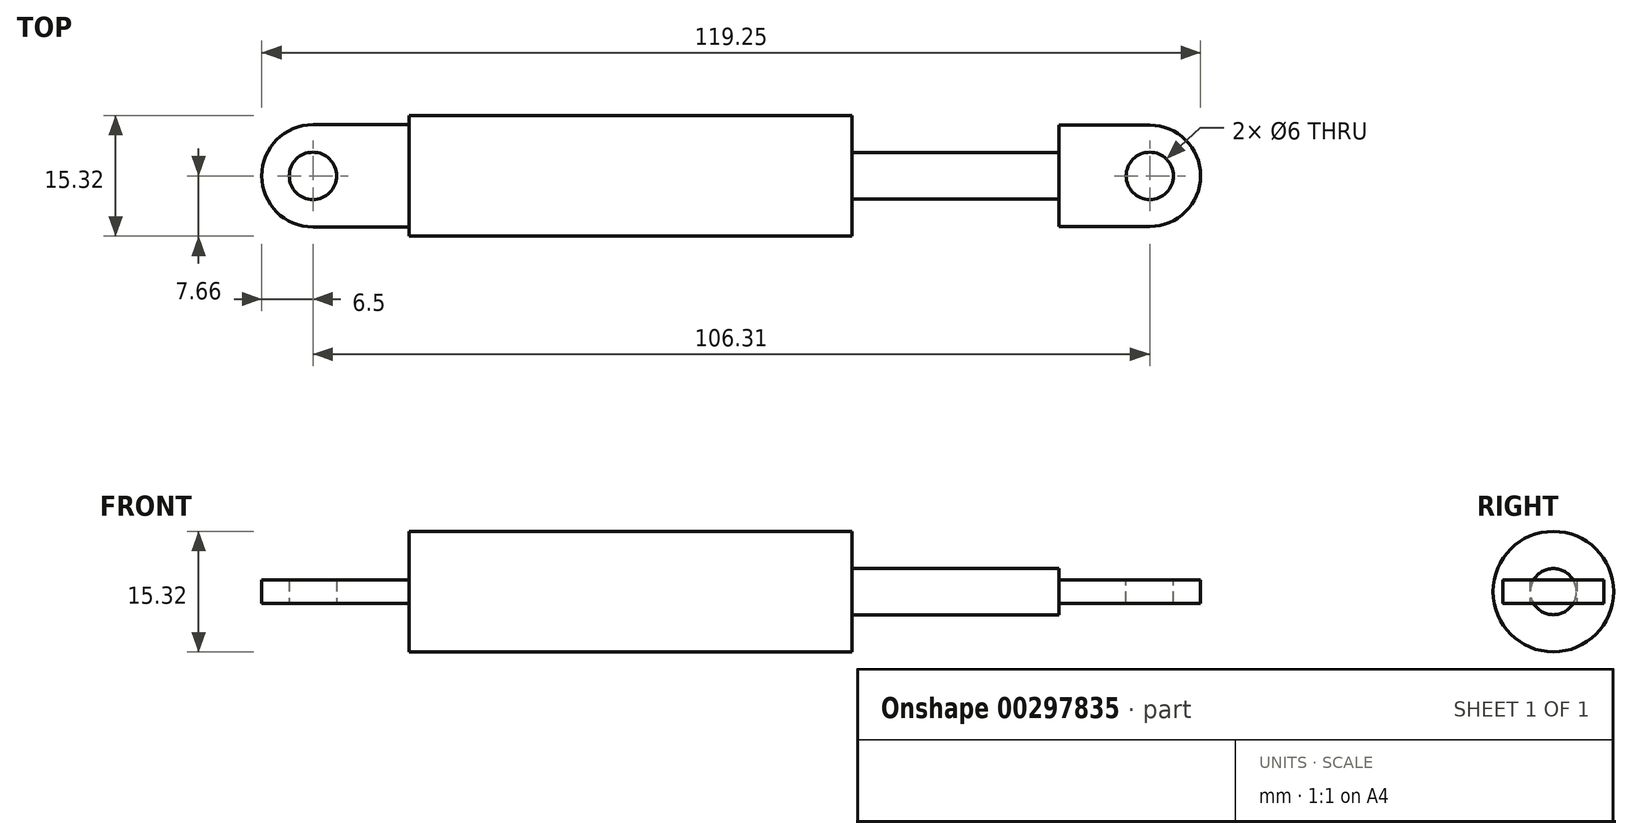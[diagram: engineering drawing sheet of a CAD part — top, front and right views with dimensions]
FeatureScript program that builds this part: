
annotation { "Feature Type Name" : "Feature", "Feature Type Description" : "" }
export const myFeature = defineFeature(function(context is Context, id is Id, definition is map)
    precondition{}
    {
        {
            var Q0;
            Q0=qCreatedBy(makeId("Top.planeOp"),FACE);
            var sketch = newSketch(context, id + "F0", { "sketchPlane" : qUnion([Q0])});
            skLineSegment(sketch, "E0.bottom", {"start": v(9.35, -6.5) * mm, "end": v(-2.85, -6.5) * mm});
            skLineSegment(sketch, "E0.top", {"start": v(9.35, 6.5) * mm, "end": v(-2.85, 6.5) * mm});
            skLineSegment(sketch, "E0.left", {"start": v(9.35, -6.5) * mm, "end": v(9.35, 6.5) * mm});
            skPoint(sketch, "E0.middle", {"position": v(0, 0) * mm});
            skArc(sketch, "E1", {"start": v(-2.85, 6.5) * mm, "mid": v(-9.35, 0) * mm, "end": v(-2.85, -6.5) * mm});
            skCircle(sketch, "E2", {"center": v(-2.85, 0) * mm, "radius": 3 * mm});
            skSolve(sketch);
        }
        {
            var Q0;
            Q0=makeQuery(id+"F0.imprint","IMPRINT",FACE,{"disambiguationData":[TD([[makeQuery(id+"F0.imprint","IMPRINT",EDGE,{"derivedFrom":sQuery(id+"F0.wireOp",EDGE,"E0.bottom")}),-1.0]])]});
            extrude(context, id + "F1", {"entities" : qUnion([Q0]), "endBound" : BoundingType.SYMMETRIC, "depth" : 3 * mm});
        }
        {
            var Q0;
            Q0=makeQuery(id+"F1.opExtrude","SWEPT_FACE",FACE,{"disambiguationData":[OSD([sQuery(id+"F0.wireOp",EDGE,"E0.left")])]});
            var sketch = newSketch(context, id + "F2", { "sketchPlane" : qUnion([Q0])});
            skCircle(sketch, "E3", {"center": v(0, 0) * mm, "radius": 7.66 * mm});
            skSolve(sketch);
        }
        {
            var Q0;
            Q0=makeQuery(id+"F2.imprint","IMPRINT",FACE,{"disambiguationData":[TD([[makeQuery(id+"F2.imprint","IMPRINT",EDGE,{"derivedFrom":sQuery(id+"F2.wireOp",EDGE,"E3")}),1.0]])]});
            var Q1;
            {var subQ0=sQuery(id+"F0.wireOp",EDGE,"E0.left");Q1=makeQuery(id+"F2.imprint","IMPRINT",FACE,{"disambiguationData":[TD([[makeQuery(id+"F2.imprint","IMPRINT",EDGE,{"derivedFrom":makeQuery(id+"F1.opExtrude","CAP_EDGE",EDGE,{"disambiguationData":[OSD([subQ0])],"isStart":true})}),1.0]])]});}
            extrude(context, id + "F3", {"entities" : qUnion([Q0, Q1]), "operationType" : NewBodyOperationType.ADD, "depth" : 56.3 * mm});
        }
        {
            var Q0;
            Q0=makeQuery(id+"F3.opExtrude","CAP_FACE",FACE,{"disambiguationData":[OSD([sQuery(id+"F2.wireOp",EDGE,"E3")])],"isStart":false});
            var sketch = newSketch(context, id + "F4", { "sketchPlane" : qUnion([Q0])});
            skCircle(sketch, "E4", {"center": v(0, 0) * mm, "radius": 2.93 * mm});
            skSolve(sketch);
        }
        {
            var Q0;
            Q0=makeQuery(id+"F4.imprint","IMPRINT",FACE,{"disambiguationData":[TD([[makeQuery(id+"F4.imprint","IMPRINT",EDGE,{"derivedFrom":sQuery(id+"F4.wireOp",EDGE,"E4")}),1.0]])]});
            extrude(context, id + "F5", {"entities" : qUnion([Q0]), "operationType" : NewBodyOperationType.ADD, "depth" : 26.25 * mm});
        }
        {
            var Q0;
            Q0=makeQuery(id+"F5.opExtrude","CAP_FACE",FACE,{"disambiguationData":[OSD([sQuery(id+"F4.wireOp",EDGE,"E4")])],"isStart":false});
            var sketch = newSketch(context, id + "F6", { "sketchPlane" : qUnion([Q0])});
            skLineSegment(sketch, "E5.bottom", {"start": v(6.44, -1.5) * mm, "end": v(-6.44, -1.5) * mm});
            skLineSegment(sketch, "E5.top", {"start": v(6.44, 1.5) * mm, "end": v(-6.44, 1.5) * mm});
            skLineSegment(sketch, "E5.left", {"start": v(6.44, -1.5) * mm, "end": v(6.44, 1.5) * mm});
            skLineSegment(sketch, "E5.right", {"start": v(-6.44, -1.5) * mm, "end": v(-6.44, 1.5) * mm});
            skPoint(sketch, "E5.middle", {"position": v(0, 0) * mm});
            skSolve(sketch);
        }
        {
            var Q0;
            {var subQ0=sQuery(id+"F6.wireOp",EDGE,"E5.left");Q0=makeQuery(id+"F6.imprint","IMPRINT",FACE,{"disambiguationData":[TD([[makeQuery(id+"F6.imprint","IMPRINT",EDGE,{"derivedFrom":subQ0}),1.0]])]});}
            var Q1;
            {var subQ0=sQuery(id+"F6.wireOp",EDGE,"E5.bottom");var subQ1=makeQuery(id+"F5.opExtrude","CAP_EDGE",EDGE,{"disambiguationData":[OSD([sQuery(id+"F4.wireOp",EDGE,"E4")])],"isStart":false});var subQ2=makeQuery(id+"F6.imprint","INTERSECT",VERTEX,{"disambiguationData":[OD(0.0)],"derivedFrom":[subQ1,subQ0]});Q1=makeQuery(id+"F6.imprint","IMPRINT",FACE,{"disambiguationData":[TD([[makeQuery(id+"F6.imprint","IMPRINT",EDGE,{"disambiguationData":[TD([[subQ2,-1.0]])],"derivedFrom":subQ0}),-1.0]])]});}
            var Q2;
            {var subQ0=sQuery(id+"F6.wireOp",EDGE,"E5.right");Q2=makeQuery(id+"F6.imprint","IMPRINT",FACE,{"disambiguationData":[TD([[makeQuery(id+"F6.imprint","IMPRINT",EDGE,{"derivedFrom":subQ0}),-1.0]])]});}
            extrude(context, id + "F7", {"entities" : qUnion([Q0, Q1, Q2]), "operationType" : NewBodyOperationType.ADD, "depth" : 18 * mm});
        }
        {
            var Q0;
            Q0=makeQuery(id+"F7.opExtrude","SWEPT_FACE",FACE,{"disambiguationData":[OSD([sQuery(id+"F6.wireOp",EDGE,"E5.top")])]});
            var sketch = newSketch(context, id + "F8", { "sketchPlane" : qUnion([Q0])});
            skPoint(sketch, "E6.endSnap0", {"position": v(109.9, 0) * mm});
            skArc(sketch, "E7", {"start": v(103.46, -6.44) * mm, "mid": v(109.9, 0) * mm, "end": v(103.46, 6.44) * mm});
            skLineSegment(sketch, "E8", {"start": v(103.46, 6.44) * mm, "end": v(109.9, 6.44) * mm});
            skLineSegment(sketch, "E9", {"start": v(109.9, 6.44) * mm, "end": v(109.9, -6.44) * mm});
            skLineSegment(sketch, "E10", {"start": v(109.9, -6.44) * mm, "end": v(103.46, -6.44) * mm});
            skCircle(sketch, "E11", {"center": v(103.46, 0) * mm, "radius": 3 * mm});
            skSolve(sketch);
        }
        {
            var Q0;
            Q0=makeQuery(id+"F8.imprint","IMPRINT",FACE,{"disambiguationData":[TD([[makeQuery(id+"F8.imprint","IMPRINT",EDGE,{"derivedFrom":sQuery(id+"F8.wireOp",EDGE,"E11")}),1.0]])]});
            var Q1;
            {var subQ0=sQuery(id+"F8.wireOp",EDGE,"E8");Q1=makeQuery(id+"F8.imprint","IMPRINT",FACE,{"disambiguationData":[TD([[makeQuery(id+"F8.imprint","IMPRINT",EDGE,{"derivedFrom":subQ0}),1.0]])]});}
            var Q2;
            {var subQ0=sQuery(id+"F8.wireOp",EDGE,"E10");Q2=makeQuery(id+"F8.imprint","IMPRINT",FACE,{"disambiguationData":[TD([[makeQuery(id+"F8.imprint","IMPRINT",EDGE,{"derivedFrom":subQ0}),-1.0]])]});}
            extrude(context, id + "F9", {"entities" : qUnion([Q0, Q1, Q2]), "operationType" : NewBodyOperationType.REMOVE, "endBound" : BoundingType.THROUGH_ALL, "oppositeDirection" : true, "depth" : 25 * mm});
        }
    });
